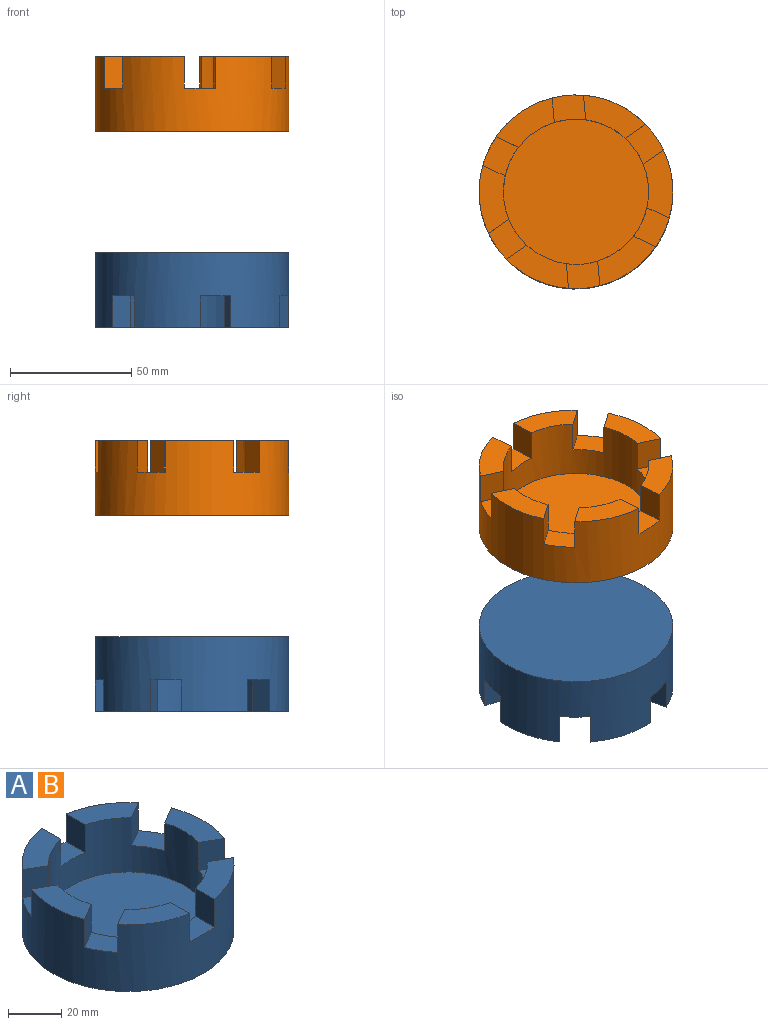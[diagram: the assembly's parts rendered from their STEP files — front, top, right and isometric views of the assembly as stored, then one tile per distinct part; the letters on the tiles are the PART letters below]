
ASSEMBLY  parts=2 mates=1
PART A: 28 faces, bbox 80x80x30.8 mm
  f0: cylinder r=30mm len=60mm, axis (0,0,-1), area 3698.9mm2, adj f1,f2,f3,f4,f5,f7,f8,f9
  f1: plane 28.21x11.39mm, normal (0,0,1), area 235.7mm2, adj f0,f6,f20,f24
  f2: plane 24.43x19.2mm, normal (0,0,1), area 235.7mm2, adj f0,f6,f17,f21
  f3: plane 24.43x19.2mm, normal (0,0,1), area 235.7mm2, adj f0,f6,f14,f18
  f4: plane 28.21x11.39mm, normal (0,0,1), area 235.7mm2, adj f0,f6,f11,f15
  f5: plane 24.43x19.2mm, normal (0,0,1), area 235.7mm2, adj f0,f6,f8,f12
  f6: cylinder r=40mm len=80mm, axis (0,0,-1), area 6734.2mm2, adj f1,f2,f3,f4,f5,f7,f8,f9
  f7: plane 24.43x19.2mm, normal (0,0,1), area 235.7mm2, adj f0,f6,f9,f23
  f8: plane 12.89x10.18mm, normal (1,0,0), area 131.2mm2, adj f0,f5,f6,f10
  f9: plane 12.89x10.18mm, normal (-1,0,0), area 131.2mm2, adj f0,f6,f7,f10
  f10: plane 13x10.71mm, normal (0,0,1), area 130.8mm2, adj f0,f6,f8,f9
  f11: plane 12.89x8.82mm, normal (0.5,0.87,0), area 131.2mm2, adj f0,f4,f6,f13
  f12: plane 12.89x8.82mm, normal (-0.5,-0.87,0), area 131.2mm2, adj f0,f5,f6,f13
  f13: plane 16.35x15.32mm, normal (0,0,1), area 130.8mm2, adj f0,f6,f11,f12
  f14: plane 12.89x8.82mm, normal (-0.5,0.87,0), area 131.2mm2, adj f0,f3,f6,f16
  f15: plane 12.89x8.82mm, normal (0.5,-0.87,0), area 131.2mm2, adj f0,f4,f6,f16
  f16: plane 16.35x15.32mm, normal (0,0,1), area 130.8mm2, adj f0,f6,f14,f15
  f17: plane 12.89x10.18mm, normal (-1,0,0), area 131.2mm2, adj f0,f2,f6,f19
  f18: plane 12.89x10.18mm, normal (1,0,0), area 131.2mm2, adj f0,f3,f6,f19
  f19: plane 13x10.71mm, normal (0,0,1), area 130.8mm2, adj f0,f6,f17,f18
  f20: plane 12.89x8.82mm, normal (-0.5,-0.87,0), area 131.2mm2, adj f0,f1,f6,f22
  f21: plane 12.89x8.82mm, normal (0.5,0.87,0), area 131.2mm2, adj f0,f2,f6,f22
  f22: plane 16.35x15.32mm, normal (0,0,1), area 130.8mm2, adj f0,f6,f20,f21
  f23: plane 12.89x8.82mm, normal (0.5,-0.87,0), area 131.2mm2, adj f0,f6,f7,f25
  f24: plane 12.89x8.82mm, normal (-0.5,0.87,0), area 131.2mm2, adj f0,f1,f6,f25
  f25: plane 16.35x15.32mm, normal (0,0,1), area 130.8mm2, adj f0,f6,f23,f24
  f26: plane 60x60mm, normal (0,0,1), area 2827.4mm2, adj f0
  f27: plane 80x80mm, normal (0,0,-1), area 5026.5mm2, adj f6
PART B: same geometry as A
PLACE A rot(axis=(0.99,0.12,0),180deg) t=(65.35,-28.15,-38.03)mm fixed
PLACE B rot(axis=(0,0,-1),175.1deg) t=(65.35,-28.15,23.6)mm
MATE revolute A.f0 <-> B.f0  axis (0,0,1) through (65.35,-28.15,-32.22)mm
